# Revit family: Accessory-Tissue_Holder-KOHLER-Components-K-78384
name_source: partatom
category: Specialty Equipment
revit_build: Autodesk Revit 2015 (Build: 20140606_1530(x64)
units: mm (PartAtom-declared; Revit-internal decimal feet)

## types (3) — shared parameters
ADA Compliant = No
Assembly Code = C1030200
Date Modified = 07/12/2018
Default Elevation = 42"
Description = Covered Double Toilet Tissue Holder
Height = 3 13/16"
Length = 6 3/16"
Manufacturer = KOHLER Co.
MasterFormat 1995 = 10820
MasterFormat 2004 = 10.28.13
Material = Premium Metal Construction
Product Documentation Link = http://www.us.kohler.com
Product Name = Components
Product Page URL = http://www.us.kohler.com
URL = https://www.us.kohler.com
Width = 11 9/16"

## per-type parameters (varying)
| type | Finish | Model | Type |
| CP-Polished Chrome | Kohler-Metal-CP-Polished_Chrome | K-78384-CP | 1 |
| BL-Matte Black | Kohler-Metal-BL-Matte_Black | K-78384-BL | 3 |
| TT-Titanium | Kohler-Metal-TT-Vibrant_Titanium | K-78384-TT | 4 |

## geometry (parser evidence)
native form markers: Sweep x5
no freeform markers — native parametric forms only
